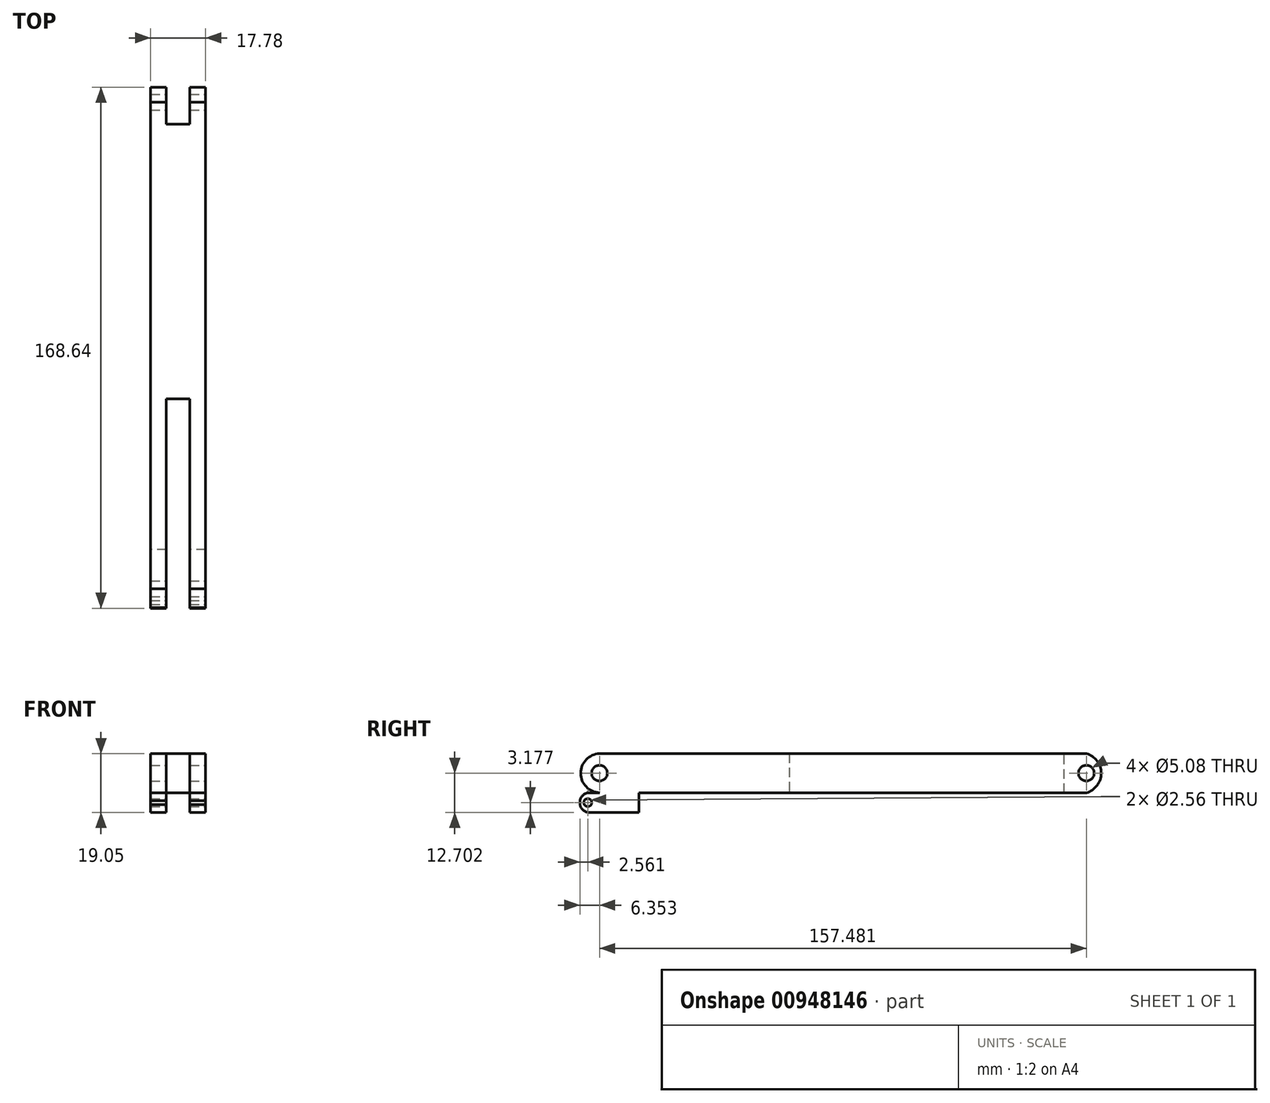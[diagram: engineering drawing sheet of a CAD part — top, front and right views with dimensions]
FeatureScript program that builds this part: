
annotation { "Feature Type Name" : "Feature", "Feature Type Description" : "" }
export const myFeature = defineFeature(function(context is Context, id is Id, definition is map)
    precondition{}
    {
        {
            var Q0;
            Q0=qCreatedBy(makeId("Right.planeOp"),FACE);
            var sketch = newSketch(context, id + "F0", { "sketchPlane" : qUnion([Q0])});
            skLineSegment(sketch, "E0.bottom", {"start": v(-21.68, 4.36) * mm, "end": v(41.82, 4.36) * mm});
            skLineSegment(sketch, "E0.top", {"start": v(-21.68, -8.34) * mm, "end": v(41.82, -8.34) * mm});
            skLineSegment(sketch, "E0.left", {"start": v(-21.68, 4.36) * mm, "end": v(-21.68, -8.34) * mm});
            skLineSegment(sketch, "E0.right", {"start": v(41.82, 4.36) * mm, "end": v(41.82, -8.34) * mm});
            skSolve(sketch);
        }
        {
            var Q0;
            Q0=makeQuery(id+"F0.imprint","IMPRINT",FACE,{"disambiguationData":[TD([[makeQuery(id+"F0.imprint","IMPRINT",EDGE,{"derivedFrom":sQuery(id+"F0.wireOp",EDGE,"E0.bottom")}),-1.0]])]});
            extrude(context, id + "F1", {"entities" : qUnion([Q0]), "depth" : 17.78 * mm, "offsetDistance" : 25.4 * mm});
        }
        {
            var Q0;
            Q0=makeQuery(id+"F1.opExtrude","SWEPT_FACE",FACE,{"disambiguationData":[OSD([sQuery(id+"F0.wireOp",EDGE,"E0.left")])]});
            var sketch = newSketch(context, id + "F2", { "sketchPlane" : qUnion([Q0])});
            skLineSegment(sketch, "E1.bottom", {"start": v(5.08, 4.36) * mm, "end": v(12.7, 4.36) * mm});
            skLineSegment(sketch, "E1.top", {"start": v(5.08, -8.34) * mm, "end": v(12.7, -8.34) * mm});
            skLineSegment(sketch, "E1.left", {"start": v(5.08, 4.36) * mm, "end": v(5.08, -8.34) * mm});
            skLineSegment(sketch, "E1.right", {"start": v(12.7, 4.36) * mm, "end": v(12.7, -8.34) * mm});
            skLineSegment(sketch, "E2", {"start": v(0, 4.36) * mm, "end": v(5.08, 4.36) * mm});
            skSolve(sketch);
        }
        {
            var Q0;
            {var subQ0=sQuery(id+"F2.wireOp",EDGE,"E1.left");Q0=makeQuery(id+"F2.imprint","IMPRINT",FACE,{"disambiguationData":[TD([[makeQuery(id+"F2.imprint","IMPRINT",EDGE,{"derivedFrom":subQ0}),-1.0]])]});}
            var Q1;
            {var subQ0=sQuery(id+"F2.wireOp",EDGE,"E1.right");Q1=makeQuery(id+"F2.imprint","IMPRINT",FACE,{"disambiguationData":[TD([[makeQuery(id+"F2.imprint","IMPRINT",EDGE,{"derivedFrom":subQ0}),1.0]])]});}
            extrude(context, id + "F3", {"entities" : qUnion([Q0, Q1]), "operationType" : NewBodyOperationType.ADD, "depth" : 25.4 * mm, "offsetDistance" : 25.4 * mm});
        }
        {
            var Q0;
            {var subQ0=sQuery(id+"F0.wireOp",EDGE,"E0.left");Q0=makeQuery(id+"F3.boolean.opBoolean","MERGE",FACE,{"derivedFrom":[makeQuery(id+"F1.opExtrude","CAP_FACE",FACE,{"disambiguationData":[OSD([sQuery(id+"F0.wireOp",EDGE,"E0.bottom"),sQuery(id+"F0.wireOp",EDGE,"E0.top"),subQ0,sQuery(id+"F0.wireOp",EDGE,"E0.right")])],"isStart":false}),makeQuery(id+"F3.opExtrude","SWEPT_FACE",FACE,{"disambiguationData":[OSD([subQ0]),TDD([makeQuery(id+"F2.imprint","IMPRINT",EDGE,{"derivedFrom":makeQuery(id+"F1.opExtrude","CAP_EDGE",EDGE,{"disambiguationData":[OSD([subQ0])],"isStart":false})})])]})]});}
            var sketch = newSketch(context, id + "F4", { "sketchPlane" : qUnion([Q0])});
            skCircle(sketch, "E3", {"center": v(-32.28, -1.99) * mm, "radius": 2.54 * mm});
            skPoint(sketch, "E3.centerSnap0", {"position": v(-47.08, -1.99) * mm});
            skArc(sketch, "E4", {"start": v(-32.28, 4.36) * mm, "mid": v(-38.35, -1.99) * mm, "end": v(-32.28, -8.34) * mm});
            skSolve(sketch);
        }
        {
            var Q0;
            Q0 = qSketchRegion(id + "F4", true);
            var Q1;
            {var subQ0=sQuery(id+"F0.wireOp",EDGE,"E0.left");var subQ1=makeQuery(id+"F1.opExtrude","CAP_EDGE",EDGE,{"disambiguationData":[OSD([subQ0])],"isStart":false});var subQ2=makeQuery(id+"F3.opExtrude","CAP_EDGE",EDGE,{"disambiguationData":[OSD([subQ0]),TDD([makeQuery(id+"F2.imprint","IMPRINT",EDGE,{"derivedFrom":subQ1})])],"isStart":false});Q1=makeQuery(id+"F4.imprint","IMPRINT",FACE,{"disambiguationData":[TD([[makeQuery(id+"F4.imprint","IMPRINT",EDGE,{"derivedFrom":subQ2}),1.0]])]});}
            extrude(context, id + "F5", {"entities" : qUnion([Q0, Q1]), "operationType" : NewBodyOperationType.REMOVE, "oppositeDirection" : true, "depth" : 25.4 * mm, "offsetDistance" : 25.4 * mm});
        }
        {
            var Q0;
            Q0=makeQuery(id+"F1.opExtrude","SWEPT_FACE",FACE,{"disambiguationData":[OSD([sQuery(id+"F0.wireOp",EDGE,"E0.left")])]});
            extrude(context, id + "F6", {"entities" : qUnion([Q0]), "operationType" : NewBodyOperationType.REMOVE, "oppositeDirection" : true, "depth" : 50.8 * mm, "offsetDistance" : 25.4 * mm});
        }
        {
            var Q0;
            Q0=makeQuery(id+"F1.opExtrude","SWEPT_FACE",FACE,{"disambiguationData":[OSD([sQuery(id+"F0.wireOp",EDGE,"E0.right")])]});
            extrude(context, id + "F7", {"entities" : qUnion([Q0]), "operationType" : NewBodyOperationType.ADD, "depth" : 76.2 * mm, "offsetDistance" : 25.4 * mm});
        }
        {
            var Q0;
            Q0=makeQuery(id+"F7.opExtrude","CAP_FACE",FACE,{"disambiguationData":[OSD([sQuery(id+"F0.wireOp",EDGE,"E0.right")])],"isStart":false});
            var sketch = newSketch(context, id + "F8", { "sketchPlane" : qUnion([Q0])});
            skLineSegment(sketch, "E5.bottom", {"start": v(-17.78, -8.34) * mm, "end": v(-12.7, -8.34) * mm});
            skLineSegment(sketch, "E5.top", {"start": v(-17.78, 4.36) * mm, "end": v(-12.7, 4.36) * mm});
            skLineSegment(sketch, "E5.left", {"start": v(-17.78, -8.34) * mm, "end": v(-17.78, 4.36) * mm});
            skLineSegment(sketch, "E5.right", {"start": v(-12.7, -8.34) * mm, "end": v(-12.7, 4.36) * mm});
            skLineSegment(sketch, "E6.bottom", {"start": v(0, 4.36) * mm, "end": v(-5.08, 4.36) * mm});
            skLineSegment(sketch, "E6.top", {"start": v(0, -8.34) * mm, "end": v(-5.08, -8.34) * mm});
            skLineSegment(sketch, "E6.left", {"start": v(0, 4.36) * mm, "end": v(0, -8.34) * mm});
            skLineSegment(sketch, "E6.right", {"start": v(-5.08, 4.36) * mm, "end": v(-5.08, -8.34) * mm});
            skSolve(sketch);
        }
        {
            var Q0;
            Q0=makeQuery(id+"F8.imprint","IMPRINT",FACE,{"disambiguationData":[TD([[makeQuery(id+"F8.imprint","IMPRINT",EDGE,{"derivedFrom":sQuery(id+"F8.wireOp",EDGE,"E5.bottom")}),1.0]])]});
            var Q1;
            Q1=makeQuery(id+"F8.imprint","IMPRINT",FACE,{"disambiguationData":[TD([[makeQuery(id+"F8.imprint","IMPRINT",EDGE,{"derivedFrom":sQuery(id+"F8.wireOp",EDGE,"E6.bottom")}),-1.0]])]});
            extrude(context, id + "F9", {"entities" : qUnion([Q0, Q1]), "operationType" : NewBodyOperationType.ADD, "depth" : 12.7 * mm, "offsetDistance" : 25.4 * mm});
        }
        {
            var Q0;
            {var subQ0=sQuery(id+"F0.wireOp",EDGE,"E0.right");var subQ1=sQuery(id+"F0.wireOp",EDGE,"E0.left");Q0=makeQuery(id+"F9.boolean.opBoolean","MERGE",FACE,{"derivedFrom":[makeQuery(id+"F7.boolean.opBoolean","MERGE",FACE,{"derivedFrom":[makeQuery(id+"F3.boolean.opBoolean","MERGE",FACE,{"derivedFrom":[makeQuery(id+"F1.opExtrude","CAP_FACE",FACE,{"disambiguationData":[OSD([sQuery(id+"F0.wireOp",EDGE,"E0.bottom"),sQuery(id+"F0.wireOp",EDGE,"E0.top"),subQ1,subQ0])],"isStart":false}),makeQuery(id+"F3.opExtrude","SWEPT_FACE",FACE,{"disambiguationData":[OSD([subQ1]),TDD([makeQuery(id+"F2.imprint","IMPRINT",EDGE,{"derivedFrom":makeQuery(id+"F1.opExtrude","CAP_EDGE",EDGE,{"disambiguationData":[OSD([subQ1])],"isStart":false})})])]})]}),makeQuery(id+"F7.opExtrude","SWEPT_FACE",FACE,{"disambiguationData":[OSD([subQ0]),TDD([makeQuery(id+"F1.opExtrude","CAP_EDGE",EDGE,{"disambiguationData":[OSD([subQ0])],"isStart":false})])]})]}),makeQuery(id+"F9.opExtrude","SWEPT_FACE",FACE,{"disambiguationData":[OSD([sQuery(id+"F8.wireOp",EDGE,"E5.left")])]})]});}
            var sketch = newSketch(context, id + "F10", { "sketchPlane" : qUnion([Q0])});
            skCircle(sketch, "E7", {"center": v(125.2, -1.99) * mm, "radius": 2.54 * mm});
            skPoint(sketch, "E7.centerSnap0", {"position": v(130.72, -1.99) * mm});
            skArc(sketch, "E8", {"start": v(125.2, -8.34) * mm, "mid": v(130, -1.99) * mm, "end": v(125.2, 4.36) * mm});
            skSolve(sketch);
        }
        {
            var Q0;
            {var subQ0=sQuery(id+"F0.wireOp",EDGE,"E0.top");var subQ1=sQuery(id+"F0.wireOp",EDGE,"E0.left");var subQ2=makeQuery(id+"F1.opExtrude","SWEPT_EDGE",EDGE,{"disambiguationData":[OSD([subQ0,subQ1])]});Q0=makeQuery(id+"F9.boolean.opBoolean","MERGE",FACE,{"derivedFrom":[makeQuery(id+"F7.boolean.opBoolean","MERGE",FACE,{"derivedFrom":[makeQuery(id+"F3.boolean.opBoolean","MERGE",FACE,{"derivedFrom":[makeQuery(id+"F1.opExtrude","SWEPT_FACE",FACE,{"disambiguationData":[OSD([subQ0])]}),makeQuery(id+"F3.opExtrude","SWEPT_FACE",FACE,{"disambiguationData":[OSD([subQ0,subQ1]),TDD([makeQuery(id+"F2.imprint","IMPRINT",EDGE,{"disambiguationData":[TD([[makeQuery(id+"F2.imprint","INTERSECT",VERTEX,{"derivedFrom":[subQ2,makeQuery(id+"F1.opExtrude","CAP_EDGE",EDGE,{"disambiguationData":[OSD([subQ1])],"isStart":true})]}),1.0]])],"derivedFrom":subQ2})])]}),makeQuery(id+"F3.opExtrude","SWEPT_FACE",FACE,{"disambiguationData":[OSD([subQ0,subQ1]),TDD([makeQuery(id+"F2.imprint","IMPRINT",EDGE,{"disambiguationData":[TD([[makeQuery(id+"F2.imprint","INTERSECT",VERTEX,{"derivedFrom":[subQ2,makeQuery(id+"F1.opExtrude","CAP_EDGE",EDGE,{"disambiguationData":[OSD([subQ1])],"isStart":false})]}),-1.0]])],"derivedFrom":subQ2})])]})]}),makeQuery(id+"F7.opExtrude","SWEPT_FACE",FACE,{"disambiguationData":[OSD([subQ0,sQuery(id+"F0.wireOp",EDGE,"E0.right")])]})]}),makeQuery(id+"F9.opExtrude","SWEPT_FACE",FACE,{"disambiguationData":[OSD([sQuery(id+"F8.wireOp",EDGE,"E5.bottom")])]}),makeQuery(id+"F9.opExtrude","SWEPT_FACE",FACE,{"disambiguationData":[OSD([sQuery(id+"F8.wireOp",EDGE,"E6.top")])]})]});}
            var sketch = newSketch(context, id + "F11", { "sketchPlane" : qUnion([Q0])});
            skLineSegment(sketch, "E9.bottom", {"start": v(17.78, 32.28) * mm, "end": v(12.7, 32.28) * mm});
            skLineSegment(sketch, "E9.top", {"start": v(17.78, 19.58) * mm, "end": v(12.7, 19.58) * mm});
            skLineSegment(sketch, "E9.left", {"start": v(17.78, 32.28) * mm, "end": v(17.78, 19.58) * mm});
            skLineSegment(sketch, "E9.right", {"start": v(12.7, 32.28) * mm, "end": v(12.7, 19.58) * mm});
            skLineSegment(sketch, "E10.bottom", {"start": v(5.08, 19.58) * mm, "end": v(0, 19.58) * mm});
            skLineSegment(sketch, "E10.top", {"start": v(5.08, 32.28) * mm, "end": v(0, 32.28) * mm});
            skLineSegment(sketch, "E10.left", {"start": v(5.08, 19.58) * mm, "end": v(5.08, 32.28) * mm});
            skLineSegment(sketch, "E10.right", {"start": v(0, 19.58) * mm, "end": v(0, 32.28) * mm});
            skSolve(sketch);
        }
        {
            var Q0;
            Q0=makeQuery(id+"F11.imprint","IMPRINT",FACE,{"disambiguationData":[TD([[makeQuery(id+"F11.imprint","IMPRINT",EDGE,{"derivedFrom":sQuery(id+"F11.wireOp",EDGE,"E9.bottom")}),-1.0]])]});
            var Q1;
            Q1=makeQuery(id+"F11.imprint","IMPRINT",FACE,{"disambiguationData":[TD([[makeQuery(id+"F11.imprint","IMPRINT",EDGE,{"derivedFrom":sQuery(id+"F11.wireOp",EDGE,"E10.bottom")}),-1.0]])]});
            extrude(context, id + "F12", {"entities" : qUnion([Q0, Q1]), "operationType" : NewBodyOperationType.ADD, "depth" : 6.35 * mm, "offsetDistance" : 25.4 * mm});
        }
        {
            var Q0;
            Q0=makeQuery(id+"F12.opExtrude","SWEPT_FACE",FACE,{"disambiguationData":[OSD([sQuery(id+"F11.wireOp",EDGE,"E9.bottom")])]});
            var Q1;
            Q1=makeQuery(id+"F12.opExtrude","SWEPT_FACE",FACE,{"disambiguationData":[OSD([sQuery(id+"F11.wireOp",EDGE,"E10.top")])]});
            extrude(context, id + "F13", {"entities" : qUnion([Q0, Q1]), "operationType" : NewBodyOperationType.ADD, "depth" : 6.35 * mm, "offsetDistance" : 25.4 * mm});
        }
        {
            var Q0;
            {var subQ0=sQuery(id+"F11.wireOp",EDGE,"E9.left");var subQ1=sQuery(id+"F0.wireOp",EDGE,"E0.right");var subQ2=sQuery(id+"F0.wireOp",EDGE,"E0.left");Q0=makeQuery(id+"F13.boolean.opBoolean","MERGE",FACE,{"derivedFrom":[makeQuery(id+"F12.boolean.opBoolean","MERGE",FACE,{"derivedFrom":[makeQuery(id+"F9.boolean.opBoolean","MERGE",FACE,{"derivedFrom":[makeQuery(id+"F7.boolean.opBoolean","MERGE",FACE,{"derivedFrom":[makeQuery(id+"F3.boolean.opBoolean","MERGE",FACE,{"derivedFrom":[makeQuery(id+"F1.opExtrude","CAP_FACE",FACE,{"disambiguationData":[OSD([sQuery(id+"F0.wireOp",EDGE,"E0.bottom"),sQuery(id+"F0.wireOp",EDGE,"E0.top"),subQ2,subQ1])],"isStart":false}),makeQuery(id+"F3.opExtrude","SWEPT_FACE",FACE,{"disambiguationData":[OSD([subQ2]),TDD([makeQuery(id+"F2.imprint","IMPRINT",EDGE,{"derivedFrom":makeQuery(id+"F1.opExtrude","CAP_EDGE",EDGE,{"disambiguationData":[OSD([subQ2])],"isStart":false})})])]})]}),makeQuery(id+"F7.opExtrude","SWEPT_FACE",FACE,{"disambiguationData":[OSD([subQ1]),TDD([makeQuery(id+"F1.opExtrude","CAP_EDGE",EDGE,{"disambiguationData":[OSD([subQ1])],"isStart":false})])]})]}),makeQuery(id+"F9.opExtrude","SWEPT_FACE",FACE,{"disambiguationData":[OSD([sQuery(id+"F8.wireOp",EDGE,"E5.left")])]})]}),makeQuery(id+"F12.opExtrude","SWEPT_FACE",FACE,{"disambiguationData":[OSD([subQ0])]})]}),makeQuery(id+"F13.opExtrude","SWEPT_FACE",FACE,{"disambiguationData":[OSD([sQuery(id+"F11.wireOp",EDGE,"E9.bottom"),subQ0])]})]});}
            var sketch = newSketch(context, id + "F14", { "sketchPlane" : qUnion([Q0])});
            skArc(sketch, "E11", {"start": v(-36.07, -8.34) * mm, "mid": v(-38.69, -11.51) * mm, "end": v(-36.07, -14.69) * mm});
            skCircle(sketch, "E12", {"center": v(-36.07, -11.51) * mm, "radius": 1.28 * mm});
            skPoint(sketch, "E12.centerSnap0", {"position": v(-38.63, -11.51) * mm});
            skSolve(sketch);
        }
        {
            var Q0;
            {var subQ0=sQuery(id+"F14.wireOp",EDGE,"iE4yJ1zb-f8u2-gCx0-1HA1-j052npTCBpgm");Q0=makeQuery(id+"F14.imprint","IMPRINT",FACE,{"disambiguationData":[TD([[makeQuery(id+"F14.imprint","IMPRINT",EDGE,{"derivedFrom":subQ0}),-1.0]])]});}
            var Q1;
            Q1=makeQuery(id+"F14.imprint","IMPRINT",FACE,{"disambiguationData":[TD([[makeQuery(id+"F14.imprint","IMPRINT",EDGE,{"derivedFrom":sQuery(id+"F14.wireOp",EDGE,"dkXmPxXi-ojEB-4lZF-Abu1-lDuEWZ0fXulm")}),1.0]])]});
            var Q2;
            {var subQ0=sQuery(id+"F14.wireOp",EDGE,"E11");Q2=makeQuery(id+"F14.imprint","IMPRINT",FACE,{"disambiguationData":[TD([[makeQuery(id+"F14.imprint","IMPRINT",EDGE,{"derivedFrom":subQ0}),-1.0]])]});}
            extrude(context, id + "F15", {"entities" : qUnion([Q0, Q1, Q2]), "operationType" : NewBodyOperationType.REMOVE, "oppositeDirection" : true, "depth" : 25.4 * mm, "offsetDistance" : 25.4 * mm});
        }
        {
            var Q0;
            {var subQ0=sQuery(id+"F10.wireOp",EDGE,"E8");Q0=makeQuery(id+"F10.imprint","IMPRINT",FACE,{"disambiguationData":[TD([[makeQuery(id+"F10.imprint","IMPRINT",EDGE,{"derivedFrom":subQ0}),-1.0]])]});}
            var Q1;
            Q1=makeQuery(id+"F10.imprint","IMPRINT",FACE,{"disambiguationData":[TD([[makeQuery(id+"F10.imprint","IMPRINT",EDGE,{"derivedFrom":sQuery(id+"F10.wireOp",EDGE,"E7")}),1.0]])]});
            extrude(context, id + "F16", {"entities" : qUnion([Q0, Q1]), "operationType" : NewBodyOperationType.REMOVE, "oppositeDirection" : true, "depth" : 25.4 * mm, "offsetDistance" : 25.4 * mm});
        }
        {
            var Q0;
            Q0 = qSketchRegion(id + "F14", true);
            extrude(context, id + "F17", {"entities" : qUnion([Q0]), "operationType" : NewBodyOperationType.REMOVE, "oppositeDirection" : true, "depth" : 25.4 * mm, "offsetDistance" : 25.4 * mm});
        }
    });
